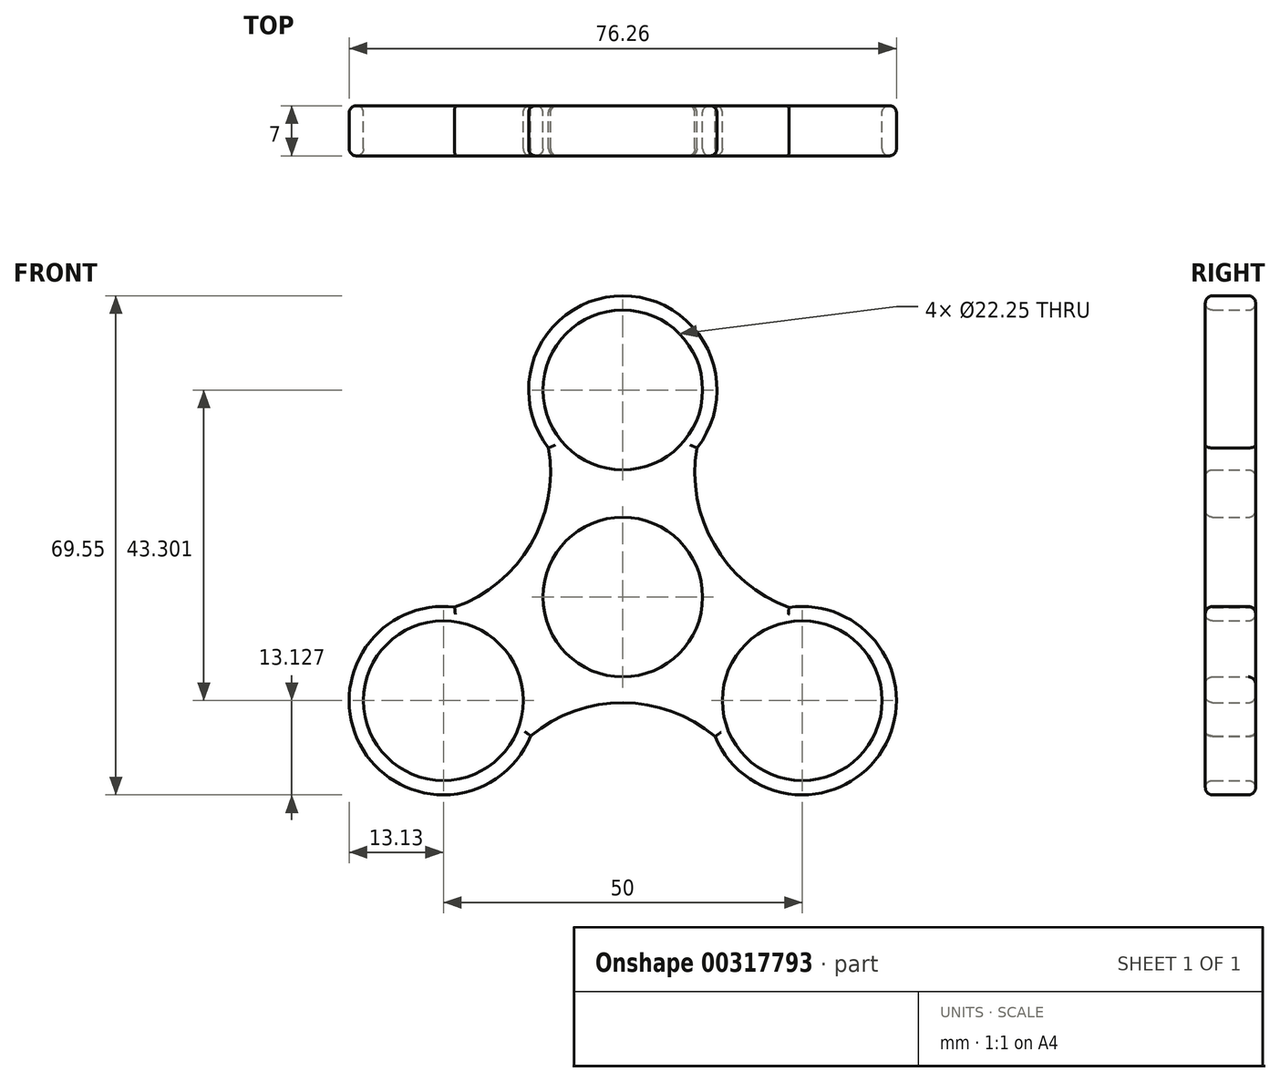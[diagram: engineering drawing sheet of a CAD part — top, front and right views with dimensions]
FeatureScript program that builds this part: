
annotation { "Feature Type Name" : "Feature", "Feature Type Description" : "" }
export const myFeature = defineFeature(function(context is Context, id is Id, definition is map)
    precondition{}
    {
        {
            var Q0;
            Q0=qCreatedBy(makeId("Front.planeOp"),FACE);
            var sketch = newSketch(context, id + "F0", { "sketchPlane" : qUnion([Q0])});
            skCircle(sketch, "E0", {"center": v(0, 29.8) * mm, "radius": 11.13 * mm});
            skCircle(sketch, "E1", {"center": v(25, -13.5) * mm, "radius": 11.13 * mm});
            skCircle(sketch, "E2", {"center": v(-25, -13.5) * mm, "radius": 11.13 * mm});
            skCircle(sketch, "E3", {"center": v(0, 29.8) * mm, "radius": 13.12 * mm});
            skCircle(sketch, "E4", {"center": v(-25, -13.5) * mm, "radius": 13.12 * mm});
            skCircle(sketch, "E5", {"center": v(25, -13.5) * mm, "radius": 13.12 * mm});
            skLineSegment(sketch, "E6", {"start": v(0, 29.8) * mm, "end": v(25, -13.5) * mm, "construction": true});
            skLineSegment(sketch, "E7", {"start": v(0, 29.8) * mm, "end": v(-25, -13.5) * mm, "construction": true});
            skLineSegment(sketch, "E8", {"start": v(25, -13.5) * mm, "end": v(-25, -13.5) * mm, "construction": true});
            skPoint(sketch, "E9", {"position": v(0, 0.94) * mm});
            skCircle(sketch, "E10", {"center": v(0, 0.94) * mm, "radius": 11.12 * mm});
            skPoint(sketch, "E11", {"position": v(10.34, 21.72) * mm});
            skPoint(sketch, "E12", {"position": v(23.16, -0.5) * mm});
            skArc(sketch, "E13", {"start": v(10.34, 21.72) * mm, "mid": v(12.72, 8.28) * mm, "end": v(23.16, -0.5) * mm});
            skPoint(sketch, "E14", {"position": v(-10.34, 21.72) * mm});
            skPoint(sketch, "E15", {"position": v(-23.44, -0.46) * mm});
            skArc(sketch, "E16", {"start": v(-23.44, -0.46) * mm, "mid": v(-12.84, 8.24) * mm, "end": v(-10.34, 21.72) * mm});
            skPoint(sketch, "E17", {"position": v(-12.83, -18.4) * mm});
            skPoint(sketch, "E18", {"position": v(12.86, -18.5) * mm});
            skArc(sketch, "E19", {"start": v(12.86, -18.5) * mm, "mid": v(0.04, -13.78) * mm, "end": v(-12.83, -18.4) * mm});
            skSolve(sketch);
        }
        {
            var Q0;
            Q0=qSketchRegion(id+"F0",true);
            extrude(context, id + "F1", {"entities" : qUnion([Q0]), "depth" : 7 * mm});
        }
        {
            var Q0;
            Q0=makeQuery(id+"F1.opExtrude","CAP_FACE",FACE,{"disambiguationData":[OSD([sQuery(id+"F0.wireOp",EDGE,"E0"),sQuery(id+"F0.wireOp",EDGE,"E1"),sQuery(id+"F0.wireOp",EDGE,"E2"),sQuery(id+"F0.wireOp",EDGE,"E3"),sQuery(id+"F0.wireOp",EDGE,"E4"),sQuery(id+"F0.wireOp",EDGE,"E5"),sQuery(id+"F0.wireOp",EDGE,"E10"),sQuery(id+"F0.wireOp",EDGE,"E13"),sQuery(id+"F0.wireOp",EDGE,"E16"),sQuery(id+"F0.wireOp",EDGE,"E19")])],"isStart":true});
            var Q1;
            Q1=makeQuery(id+"F1.opExtrude","CAP_FACE",FACE,{"disambiguationData":[OSD([sQuery(id+"F0.wireOp",EDGE,"E0"),sQuery(id+"F0.wireOp",EDGE,"E1"),sQuery(id+"F0.wireOp",EDGE,"E2"),sQuery(id+"F0.wireOp",EDGE,"E3"),sQuery(id+"F0.wireOp",EDGE,"E4"),sQuery(id+"F0.wireOp",EDGE,"E5"),sQuery(id+"F0.wireOp",EDGE,"E10"),sQuery(id+"F0.wireOp",EDGE,"E13"),sQuery(id+"F0.wireOp",EDGE,"E16"),sQuery(id+"F0.wireOp",EDGE,"E19")])],"isStart":false});
            fillet(context, id + "F2", {"entities" : qUnion([Q0, Q1]), "radius" : 1 * mm, "tangentPropagation" : true, "allowEdgeOverflow" : false});
        }
    });
